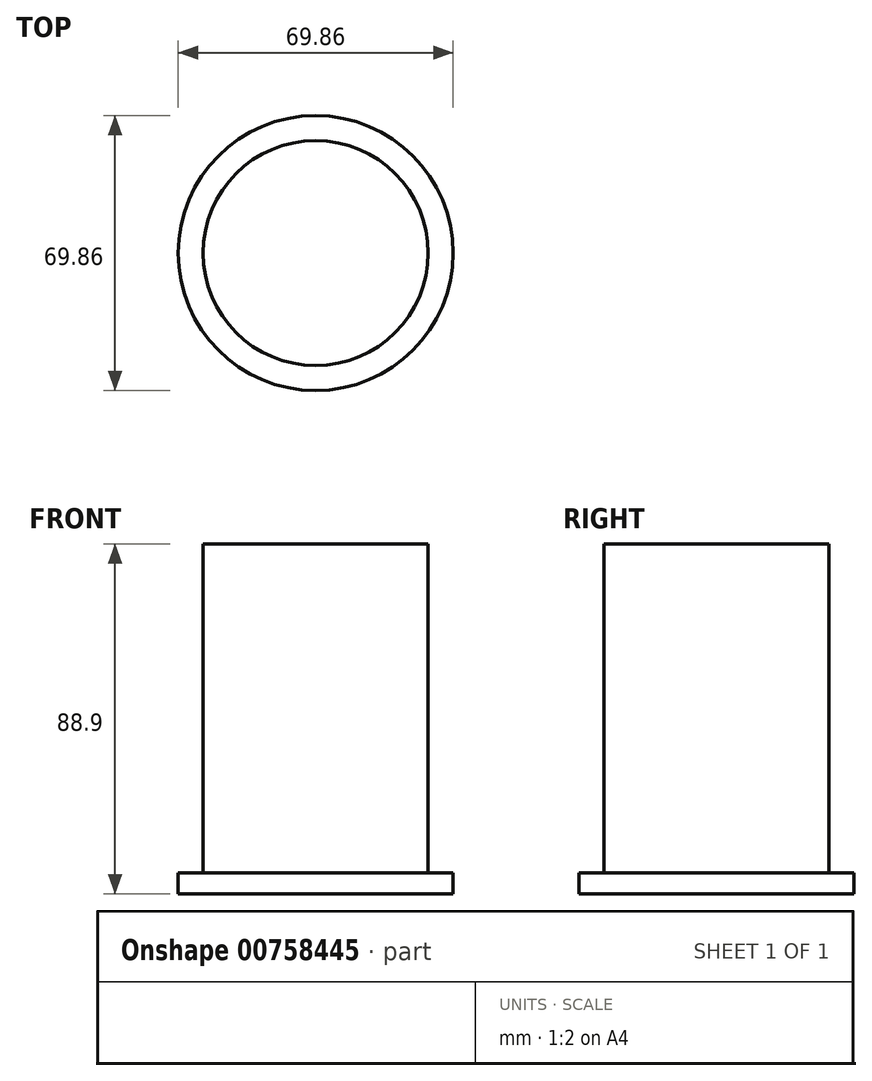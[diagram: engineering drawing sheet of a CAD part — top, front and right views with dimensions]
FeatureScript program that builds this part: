
annotation { "Feature Type Name" : "Feature", "Feature Type Description" : "" }
export const myFeature = defineFeature(function(context is Context, id is Id, definition is map)
    precondition{}
    {
        {
            var Q0;
            Q0=qCreatedBy(makeId("Top.planeOp"),FACE);
            var sketch = newSketch(context, id + "F0", { "sketchPlane" : qUnion([Q0])});
            skCircle(sketch, "E0", {"center": v(0, 0) * mm, "radius": 34.93 * mm});
            skSolve(sketch);
        }
        {
            var Q0;
            Q0=makeQuery(id+"F0.imprint","IMPRINT",FACE,{"disambiguationData":[TD([[makeQuery(id+"F0.imprint","IMPRINT",EDGE,{"derivedFrom":sQuery(id+"F0.wireOp",EDGE,"E0")}),1.0]])]});
            extrude(context, id + "F1", {"entities" : qUnion([Q0]), "depth" : 88.9 * mm, "offsetDistance" : 25.4 * mm});
        }
        {
            var Q0;
            Q0=makeQuery(id+"F1.opExtrude","CAP_FACE",FACE,{"disambiguationData":[OSD([sQuery(id+"F0.wireOp",EDGE,"E0")])],"isStart":false});
            var sketch = newSketch(context, id + "F2", { "sketchPlane" : qUnion([Q0])});
            skCircle(sketch, "E1", {"center": v(0, 0) * mm, "radius": 28.58 * mm});
            skCircle(sketch, "E2.0", {"center": v(0, 0) * mm, "radius": 82.17 * mm});
            skSolve(sketch);
        }
        {
            var Q0;
            Q0 = qSketchRegion(id + "F2", true);
            extrude(context, id + "F3", {"entities" : qUnion([Q0]), "operationType" : NewBodyOperationType.REMOVE, "oppositeDirection" : true, "depth" : 83.57 * mm, "offsetDistance" : 25.4 * mm});
        }
    });
